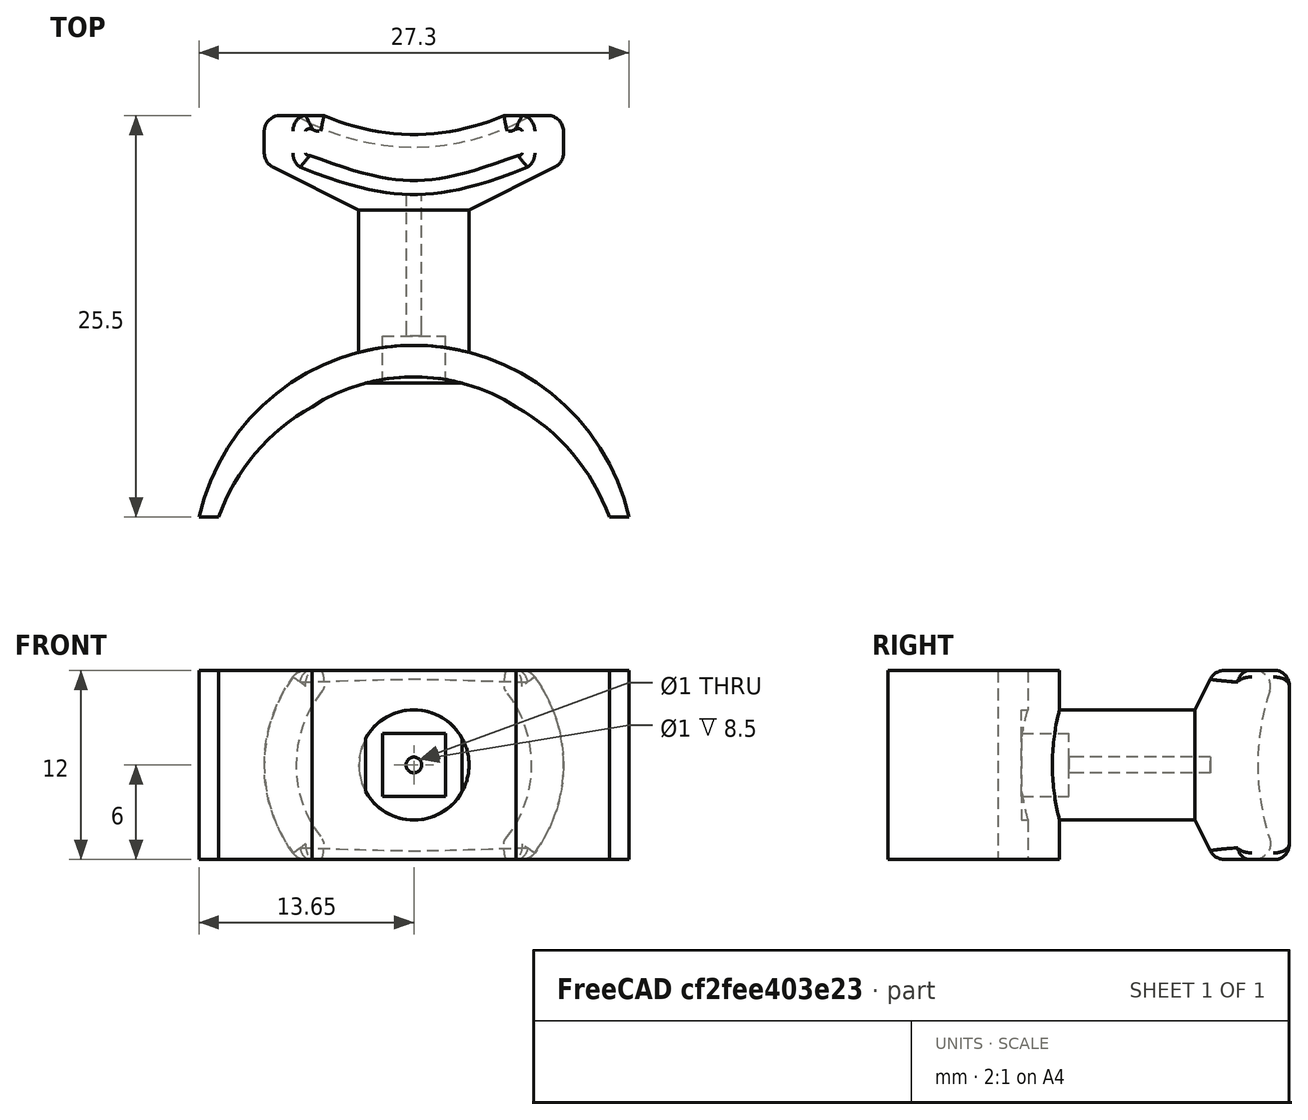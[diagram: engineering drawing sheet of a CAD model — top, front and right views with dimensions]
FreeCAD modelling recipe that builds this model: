
FCSTD DOCUMENT  (FreeCAD 0.20R26651 (Git))
Label: stick
License: All rights reserved
LicenseURL: http://en.wikipedia.org/wiki/All_rights_reserved
objects: Part::Cut×11, Part::Cylinder×10, Part::Box×5, Part::MultiFuse×4, Part::Fillet×3, Image::ImagePlane×1, Part::Cone×1, Part::Sphere×1
note: 35 computed .brp shape members not serialized (recipe doc carries the construction recipe); baked Part::Feature solids carry a one-line shape summary decoded from their .brp

FEATURE [Image::ImagePlane] ImagePlane
  XSize = 169.373
  YSize = 95.2725
FEATURE [Part::Cylinder] Cylinder  label="Zylinder"
  Angle = 180
  AttacherType = Attacher::AttachEngine3D
  FirstAngle = 0
  Height = 12
  Placement = pos=(-13,-7.6,0) rot=(0,0,1;0rad)
  Radius = 14
  SecondAngle = 0
FEATURE [Part::Cylinder] Cylinder001  label="Zylinder001"
  Angle = 180
  AttacherType = Attacher::AttachEngine3D
  FirstAngle = 0
  Height = 12
  Placement = pos=(-13,-7.6,0) rot=(0,0,1;0rad)
  Radius = 12
  SecondAngle = 0
FEATURE [Part::Cut] Cut
  Base = -> Cylinder
  Tool = -> Cylinder001
FEATURE [Part::Cylinder] Cylinder002  label="Zylinder002"
  Angle = 360
  AttacherType = Attacher::AttachEngine3D
  FirstAngle = 0
  Height = 10
  Placement = pos=(-13,5,0) rot=(-1,0,0;1.5708rad)
  Radius = 3.5
  SecondAngle = 0
FEATURE [Part::Cone] Cone  label="Kegel"
  Angle = 360
  AttacherType = Attacher::AttachEngine3D
  Height = 3
  Placement = pos=(-13,15,0) rot=(-1,0,0;1.5708rad)
  Radius1 = 3.5
  Radius2 = 9.5
FEATURE [Part::Cylinder] Cylinder003  label="Zylinder003"
  Angle = 360
  AttacherType = Attacher::AttachEngine3D
  FirstAngle = 0
  Height = 3
  Placement = pos=(-13,18,0) rot=(-1,0,0;1.5708rad)
  Radius = 9.5
  SecondAngle = 0
FEATURE [Part::Sphere] Sphere  label="Kugel"
  Angle1 = -90
  Angle2 = 90
  Angle3 = 360
  AttacherType = Attacher::AttachEngine3D
  Placement = pos=(-13,34,0) rot=(0,0,1;0rad)
  Radius = 15
FEATURE [Part::MultiFuse] Fusion
  Shapes = -> [Cylinder002,Cone,Cylinder003]
FEATURE [Part::Cut] Cut001
  Base = -> Fusion
  Tool = -> Sphere
FEATURE [Part::Fillet] Fillet
  Base = -> Cut001
  Edges = 1 edges r=1: [Edge4]
FEATURE [Part::Fillet] Fillet001
  Base = -> Fillet
  Edges = 1 edges r=1: [Edge9]
  Placement = pos=(0,0,6) rot=(0,0,1;0rad)
FEATURE [Part::Box] Box  label="Würfel"
  AttacherType = Attacher::AttachEngine3D
  Height = 4
  Length = 4
  Placement = pos=(-15,4,4) rot=(0,0,1;0rad)
  Width = 3
FEATURE [Part::Box] Box001  label="Würfel001"
  AttacherType = Attacher::AttachEngine3D
  Height = 4
  Length = 4
  Placement = pos=(-15,4,4) rot=(0,0,1;0rad)
  Width = 4
FEATURE [Part::Cylinder] Cylinder004  label="Zylinder004"
  Angle = 360
  AttacherType = Attacher::AttachEngine3D
  FirstAngle = 0
  Height = 8.5
  Placement = pos=(-13,7.5,6) rot=(-1,0,0;1.5708rad)
  Radius = 0.5
  SecondAngle = 0
FEATURE [Part::Cut] Cut004  label="Cover_1"
  Base = -> Cut
  Tool = -> Box001
FEATURE [Part::Box] Box002  label="Würfel002"
  AttacherType = Attacher::AttachEngine3D
  Height = 12
  Length = 30
  Placement = pos=(-28,-8,0) rot=(0,0,1;0rad)
  Width = 3.5
FEATURE [Part::Cut] Cut006
  Base = -> Cut004
  Tool = -> Box002
FEATURE [Part::Cylinder] Cylinder006  label="Zylinder006"
  Angle = 360
  AttacherType = Attacher::AttachEngine3D
  FirstAngle = 0
  Height = 12
  Placement = pos=(-13,-9,0) rot=(0,0,1;0rad)
  Radius = 13.2
  SecondAngle = 0
FEATURE [Part::Cut] Cut007
  Base = -> Cut006
  Tool = -> Cylinder006
FEATURE [Part::Cylinder] Cylinder007  label="Zylinder007"
  Angle = 360
  AttacherType = Attacher::AttachEngine3D
  FirstAngle = 0
  Height = 3
  Placement = pos=(-13,7,6) rot=(1,0,0;1.5708rad)
  Radius = 3.5
  SecondAngle = 0
FEATURE [Part::MultiFuse] Fusion001
  Shapes = -> [Cylinder007,Cut007]
FEATURE [Part::Cut] Cut008
  Base = -> Fusion001
  Tool = -> Box
FEATURE [Part::Cylinder] Cylinder008  label="Zylinder008"
  Angle = 360
  AttacherType = Attacher::AttachEngine3D
  FirstAngle = 0
  Height = 0.5
  Placement = pos=(-13,7.5,6) rot=(1,0,0;1.5708rad)
  Radius = 3.5
  SecondAngle = 0
FEATURE [Part::MultiFuse] Fusion002
  Shapes = -> [Cut008,Cylinder008]
FEATURE [Part::Cylinder] Cylinder009  label="Zylinder009"
  Angle = 360
  AttacherType = Attacher::AttachEngine3D
  FirstAngle = 0
  Height = 2
  Placement = pos=(-13,6,6) rot=(-1,0,0;1.5708rad)
  Radius = 0.5
  SecondAngle = 0
FEATURE [Part::Cylinder] Cylinder010  label="Zylinder010"
  Angle = 360
  AttacherType = Attacher::AttachEngine3D
  FirstAngle = 0
  Height = 2.5
  Placement = pos=(-13,7.5,6) rot=(1,0,0;1.5708rad)
  Radius = 3.5
  SecondAngle = 0
FEATURE [Part::Cut] Cut009
  Base = -> Fillet001
  Tool = -> Cylinder010
FEATURE [Part::Cut] Cut010  label="stick_2"
  Base = -> Cut009
  Tool = -> Cylinder004
FEATURE [Part::Cut] Cut011  label="cover"
  Base = -> Fusion002
  Tool = -> Cylinder009
FEATURE [Part::Box] Box003  label="Würfel003"
  AttacherType = Attacher::AttachEngine3D
  Height = 5
  Length = 20
  Placement = pos=(-23,12,-5) rot=(0,0,1;0rad)
  Width = 10
FEATURE [Part::Cut] Cut012
  Base = -> Cut010
  Tool = -> Box003
FEATURE [Part::Box] Box004  label="Würfel004"
  AttacherType = Attacher::AttachEngine3D
  Height = 5
  Length = 20
  Placement = pos=(-23,12,12) rot=(0,0,1;0rad)
  Width = 10
FEATURE [Part::Cut] Cut013
  Base = -> Cut012
  Tool = -> Box004
FEATURE [Part::Fillet] Fillet002  label="stick"
  Base = -> Cut013
  Edges = 20 edges r=1: [Edge1,Edge3,Edge5,Edge6,Edge7,Edge8,Edge9,Edge10,Edge11,Edge12,Edge13,Edge14,Edge16,Edge17,Edge18,Edge19,Edge20,Edge21,Edge22,Edge23]
FEATURE [Part::MultiFuse] Fusion003  label="stick_complete"
  Shapes = -> [Cut011,Fillet002]
